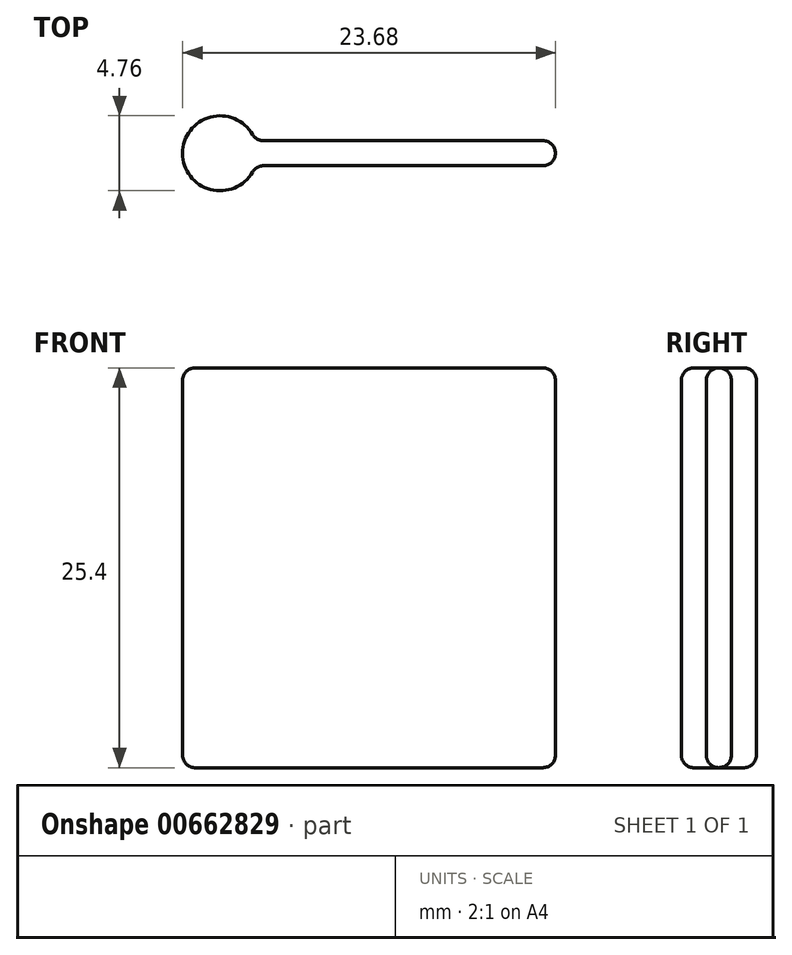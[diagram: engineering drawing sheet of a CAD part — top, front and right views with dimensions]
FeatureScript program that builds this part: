
annotation { "Feature Type Name" : "Feature", "Feature Type Description" : "" }
export const myFeature = defineFeature(function(context is Context, id is Id, definition is map)
    precondition{}
    {
        {
            var Q0;
            Q0=qCreatedBy(makeId("Top.planeOp"),FACE);
            var sketch = newSketch(context, id + "F0", { "sketchPlane" : qUnion([Q0])});
            skCircle(sketch, "E0", {"center": v(0, 0) * mm, "radius": 2.38 * mm});
            skLineSegment(sketch, "E1", {"start": v(2.25, 0.8) * mm, "end": v(21.3, 0.8) * mm});
            skLineSegment(sketch, "E2", {"start": v(21.3, 0.8) * mm, "end": v(21.3, 0) * mm});
            skLineSegment(sketch, "E3", {"start": v(-2.38, 0) * mm, "end": v(2.38, 0) * mm, "construction": true});
            skLineSegment(sketch, "E4.MirrorCS", {"start": v(2.25, -0.8) * mm, "end": v(21.3, -0.8) * mm});
            skLineSegment(sketch, "E5.MirrorCS", {"start": v(21.3, -0.8) * mm, "end": v(21.3, 0) * mm});
            skSolve(sketch);
        }
        {
            var Q0;
            {var subQ0=sQuery(id+"F0.wireOp",EDGE,"E0");var subQ1=makeQuery(id+"F0.imprint","INTERSECT",VERTEX,{"derivedFrom":[subQ0,sQuery(id+"F0.wireOp",EDGE,"HgG0rMNY-bSjj-gmUH-4ZFr-CjmrUW0QuaIE")]});Q0=makeQuery(id+"F0.imprint","IMPRINT",FACE,{"disambiguationData":[TD([[makeQuery(id+"F0.imprint","IMPRINT",EDGE,{"disambiguationData":[TD([[subQ1,-1.0]])],"derivedFrom":subQ0}),1.0]])]});}
            var Q1;
            {var subQ0=sQuery(id+"F0.wireOp",EDGE,"HgG0rMNY-bSjj-gmUH-4ZFr-CjmrUW0QuaIE");Q1=makeQuery(id+"F0.imprint","IMPRINT",FACE,{"disambiguationData":[TD([[makeQuery(id+"F0.imprint","IMPRINT",EDGE,{"derivedFrom":subQ0}),1.0]])]});}
            var Q2;
            {var subQ1=sQuery(id+"F0.wireOp",EDGE,"E1");Q2=makeQuery(id+"F0.imprint","IMPRINT",FACE,{"disambiguationData":[TD([[makeQuery(id+"F0.imprint","IMPRINT",EDGE,{"derivedFrom":subQ1}),-1.0]])]});}
            extrude(context, id + "F1", {"entities" : qUnion([Q0, Q1, Q2]), "depth" : 25.4 * mm, "offsetDistance" : 25.4 * mm});
        }
        {
            var Q0;
            Q0=makeQuery(id+"F1.opExtrude","CAP_FACE",FACE,{"disambiguationData":[OSD([sQuery(id+"F0.wireOp",EDGE,"E0"),sQuery(id+"F0.wireOp",EDGE,"E1"),sQuery(id+"F0.wireOp",EDGE,"E2"),sQuery(id+"F0.wireOp",EDGE,"E4.MirrorCS"),sQuery(id+"F0.wireOp",EDGE,"E5.MirrorCS")])],"isStart":false});
            var Q1;
            Q1=makeQuery(id+"F1.opExtrude","CAP_FACE",FACE,{"disambiguationData":[OSD([sQuery(id+"F0.wireOp",EDGE,"E0"),sQuery(id+"F0.wireOp",EDGE,"E1"),sQuery(id+"F0.wireOp",EDGE,"E2"),sQuery(id+"F0.wireOp",EDGE,"E4.MirrorCS"),sQuery(id+"F0.wireOp",EDGE,"E5.MirrorCS")])],"isStart":true});
            var Q2;
            Q2=makeQuery(id+"F1.opExtrude","SWEPT_FACE",FACE,{"disambiguationData":[OSD([sQuery(id+"F0.wireOp",EDGE,"E1")])]});
            var Q3;
            Q3=makeQuery(id+"F1.opExtrude","SWEPT_FACE",FACE,{"disambiguationData":[OSD([sQuery(id+"F0.wireOp",EDGE,"E4.MirrorCS")])]});
            fillet(context, id + "F2", {"entities" : qUnion([Q0, Q1, Q2, Q3]), "radius" : 0.8 * mm, "tangentPropagation" : true, "allowEdgeOverflow" : false});
        }
    });
